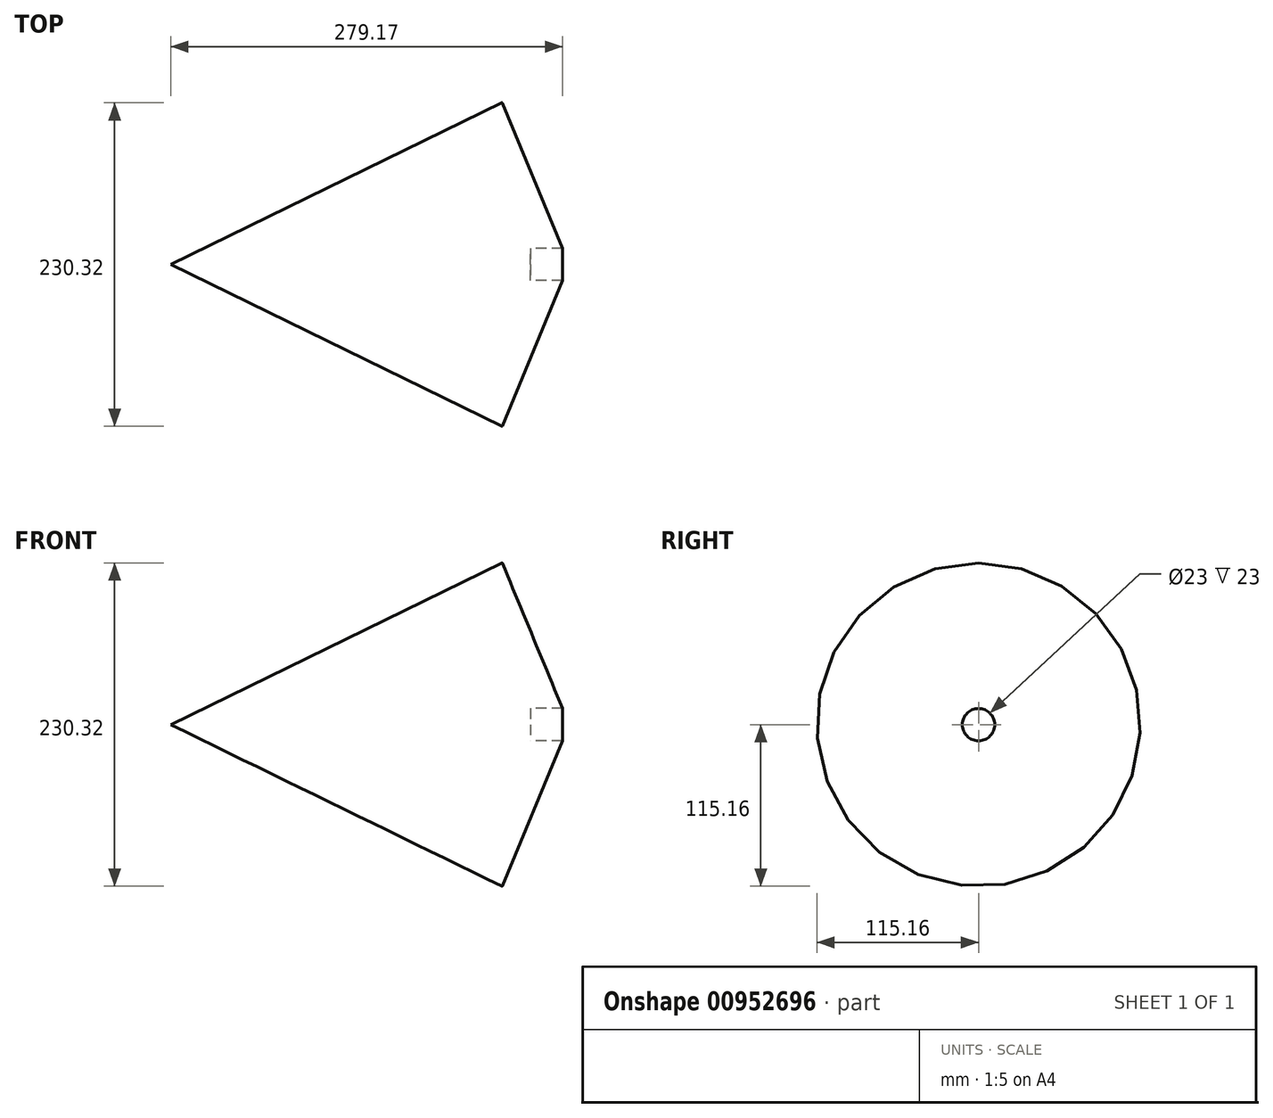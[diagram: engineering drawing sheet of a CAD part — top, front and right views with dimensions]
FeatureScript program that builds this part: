
annotation { "Feature Type Name" : "Feature", "Feature Type Description" : "" }
export const myFeature = defineFeature(function(context is Context, id is Id, definition is map)
    precondition{}
    {
        {
            var Q0;
            Q0=qCreatedBy(makeId("Front.planeOp"),FACE);
            var sketch = newSketch(context, id + "F0", { "sketchPlane" : qUnion([Q0])});
            skLineSegment(sketch, "E0", {"start": v(0, 0) * mm, "end": v(236.1, 115.15) * mm});
            skLineSegment(sketch, "E1", {"start": v(0, 0) * mm, "end": v(184.58, 0) * mm, "construction": true});
            skLineSegment(sketch, "E2", {"start": v(236.26, 115.09) * mm, "end": v(279.17, 11.5) * mm});
            skLineSegment(sketch, "E3", {"start": v(279.17, 11.5) * mm, "end": v(256.17, 11.5) * mm});
            skLineSegment(sketch, "E4", {"start": v(256.17, 11.5) * mm, "end": v(256.17, 0) * mm});
            skLineSegment(sketch, "E5", {"start": v(0, 0) * mm, "end": v(256.17, 0) * mm});
            skPoint(sketch, "E6.visualSharp", {"position": v(236.21, 115.2) * mm});
            skArc(sketch, "E6.filletArc", {"start": v(236.26, 115.09) * mm, "mid": v(236.2, 115.16) * mm, "end": v(236.1, 115.15) * mm});
            skSolve(sketch);
        }
        {
            var Q0;
            Q0 = qSketchRegion(id + "F0", true);
            var Q1;
            Q1=sQuery(id+"F0.wireOp",EDGE,"E5");
            revolve(context, id + "F1", {"surfaceOperationType" : NewSurfaceOperationType.NEW, "entities" : qUnion([Q0]), "axis" : qUnion([Q1]), "revolveType" : RevolveType.FULL});
        }
        {
            var Q0;
            Q0=qCreatedBy(makeId("Right.planeOp"),FACE);
            cPlane(context, id + "F2", {"entities" : qUnion([Q0]), "cplaneType" : CPlaneType.OFFSET, "offset" : 1600 * mm, "oppositeDirection" : true, "width" : 152.4 * mm, "height" : 152.4 * mm});
        }
    });
